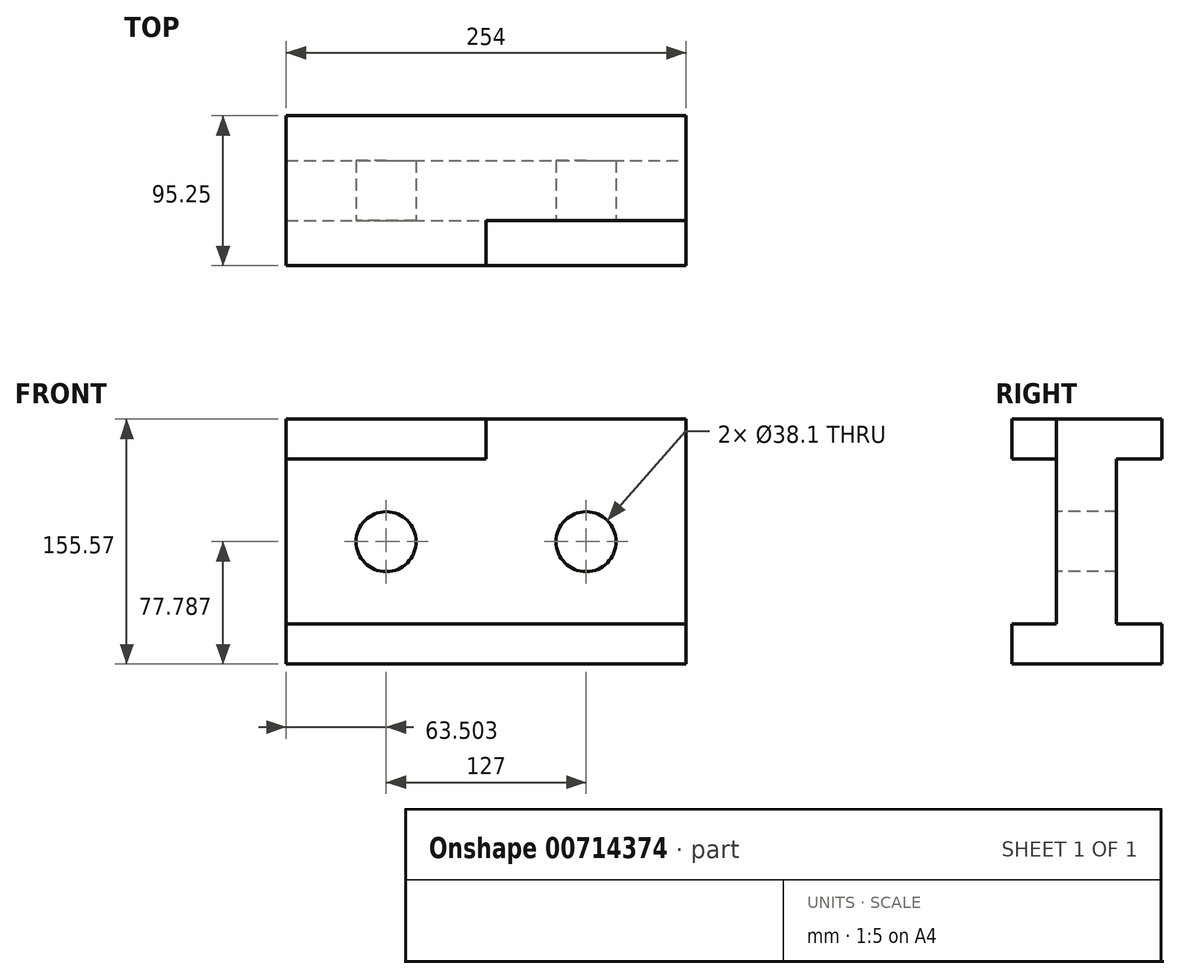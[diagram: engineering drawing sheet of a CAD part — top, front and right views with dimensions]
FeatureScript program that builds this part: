
annotation { "Feature Type Name" : "Feature", "Feature Type Description" : "" }
export const myFeature = defineFeature(function(context is Context, id is Id, definition is map)
    precondition{}
    {
        {
            var Q0;
            Q0=qCreatedBy(makeId("Front.planeOp"),FACE);
            var sketch = newSketch(context, id + "F0", { "sketchPlane" : qUnion([Q0])});
            skLineSegment(sketch, "E0.bottom", {"start": v(-135.4, 43.15) * mm, "end": v(118.6, 43.15) * mm});
            skLineSegment(sketch, "E0.top", {"start": v(-135.4, -112.42) * mm, "end": v(118.6, -112.42) * mm});
            skLineSegment(sketch, "E0.left", {"start": v(-135.4, 43.15) * mm, "end": v(-135.4, -112.42) * mm});
            skLineSegment(sketch, "E0.right", {"start": v(118.6, 43.15) * mm, "end": v(118.6, -112.42) * mm});
            skSolve(sketch);
        }
        {
            var Q0;
            Q0=qSketchRegion(id+"F0",true);
            extrude(context, id + "F1", {"entities" : qUnion([Q0]), "depth" : 95.25 * mm, "offsetDistance" : 25.4 * mm});
        }
        {
            var Q0;
            Q0=makeQuery(id+"F1.opExtrude","CAP_FACE",FACE,{"disambiguationData":[OSD([sQuery(id+"F0.wireOp",EDGE,"E0.bottom"),sQuery(id+"F0.wireOp",EDGE,"E0.top"),sQuery(id+"F0.wireOp",EDGE,"E0.left"),sQuery(id+"F0.wireOp",EDGE,"E0.right")])],"isStart":false});
            var sketch = newSketch(context, id + "F2", { "sketchPlane" : qUnion([Q0])});
            skLineSegment(sketch, "E1.bottom", {"start": v(-135.4, 17.75) * mm, "end": v(118.6, 17.75) * mm});
            skLineSegment(sketch, "E1.top", {"start": v(-135.4, -87.02) * mm, "end": v(118.6, -87.02) * mm});
            skLineSegment(sketch, "E1.left", {"start": v(-135.4, 17.75) * mm, "end": v(-135.4, -87.02) * mm});
            skLineSegment(sketch, "E1.right", {"start": v(118.6, 17.75) * mm, "end": v(118.6, -87.02) * mm});
            skSolve(sketch);
        }
        {
            var Q0;
            Q0=makeQuery(id+"F2.imprint","IMPRINT",FACE,{"disambiguationData":[TD([[makeQuery(id+"F2.imprint","IMPRINT",EDGE,{"derivedFrom":sQuery(id+"F2.wireOp",EDGE,"E1.bottom")}),-1.0]])]});
            extrude(context, id + "F3", {"entities" : qUnion([Q0]), "operationType" : NewBodyOperationType.REMOVE, "oppositeDirection" : true, "depth" : 28.57 * mm, "offsetDistance" : 25.4 * mm});
        }
        {
            var Q0;
            {var subQ0=sQuery(id+"F0.wireOp",EDGE,"E0.bottom");var subQ1=sQuery(id+"F0.wireOp",EDGE,"E0.right");var subQ2=sQuery(id+"F0.wireOp",EDGE,"E0.left");Q0=makeQuery(id+"F3.boolean.opBoolean","SPLIT",FACE,{"disambiguationData":[TD([makeQuery(id+"F1.opExtrude","SWEPT_FACE",FACE,{"disambiguationData":[OSD([subQ0])]})])],"derivedFrom":makeQuery(id+"F1.opExtrude","CAP_FACE",FACE,{"disambiguationData":[OSD([subQ0,sQuery(id+"F0.wireOp",EDGE,"E0.top"),subQ2,subQ1])],"isStart":false})});}
            var sketch = newSketch(context, id + "F4", { "sketchPlane" : qUnion([Q0])});
            skLineSegment(sketch, "E2.bottom", {"start": v(118.6, 17.75) * mm, "end": v(-8.4, 17.75) * mm});
            skLineSegment(sketch, "E2.top", {"start": v(118.6, 43.15) * mm, "end": v(-8.4, 43.15) * mm});
            skLineSegment(sketch, "E2.left", {"start": v(118.6, 17.75) * mm, "end": v(118.6, 43.15) * mm});
            skLineSegment(sketch, "E2.right", {"start": v(-8.4, 17.75) * mm, "end": v(-8.4, 43.15) * mm});
            skSolve(sketch);
        }
        {
            var Q0;
            Q0=qSketchRegion(id+"F4",true);
            extrude(context, id + "F5", {"entities" : qUnion([Q0]), "operationType" : NewBodyOperationType.REMOVE, "oppositeDirection" : true, "depth" : 28.57 * mm, "offsetDistance" : 25.4 * mm});
        }
        {
            var Q0;
            Q0=makeQuery(id+"F5.boolean.opBoolean","MERGE",FACE,{"derivedFrom":[makeQuery(id+"F3.boolean.opBoolean","COPY",FACE,{"derivedFrom":makeQuery(id+"F3.opExtrude","CAP_FACE",FACE,{"disambiguationData":[OSD([sQuery(id+"F2.wireOp",EDGE,"E1.bottom"),sQuery(id+"F2.wireOp",EDGE,"E1.top"),sQuery(id+"F2.wireOp",EDGE,"E1.left"),sQuery(id+"F2.wireOp",EDGE,"E1.right")])],"isStart":false})}),makeQuery(id+"F5.opExtrude","CAP_FACE",FACE,{"disambiguationData":[OSD([sQuery(id+"F4.wireOp",EDGE,"E2.bottom"),sQuery(id+"F4.wireOp",EDGE,"E2.top"),sQuery(id+"F4.wireOp",EDGE,"E2.left"),sQuery(id+"F4.wireOp",EDGE,"E2.right")])],"isStart":false})]});
            var sketch = newSketch(context, id + "F6", { "sketchPlane" : qUnion([Q0])});
            skCircle(sketch, "E3", {"center": v(-71.9, -34.63) * mm, "radius": 19.05 * mm});
            skCircle(sketch, "E4", {"center": v(55.1, -34.63) * mm, "radius": 19.05 * mm});
            skSolve(sketch);
        }
        {
            var Q0;
            Q0=makeQuery(id+"F6.imprint","IMPRINT",FACE,{"disambiguationData":[TD([[makeQuery(id+"F6.imprint","IMPRINT",EDGE,{"derivedFrom":sQuery(id+"F6.wireOp",EDGE,"E4")}),1.0]])]});
            var Q1;
            Q1=makeQuery(id+"F6.imprint","IMPRINT",FACE,{"disambiguationData":[TD([[makeQuery(id+"F6.imprint","IMPRINT",EDGE,{"derivedFrom":sQuery(id+"F6.wireOp",EDGE,"E3")}),1.0]])]});
            extrude(context, id + "F7", {"entities" : qUnion([Q0, Q1]), "operationType" : NewBodyOperationType.REMOVE, "endBound" : BoundingType.THROUGH_ALL, "oppositeDirection" : true, "depth" : 25.4 * mm, "offsetDistance" : 25.4 * mm});
        }
        {
            var Q0;
            Q0=makeQuery(id+"F1.opExtrude","SWEPT_FACE",FACE,{"disambiguationData":[OSD([sQuery(id+"F0.wireOp",EDGE,"E0.right")])]});
            var sketch = newSketch(context, id + "F8", { "sketchPlane" : qUnion([Q0])});
            skLineSegment(sketch, "E5.bottom", {"start": v(0, -87.02) * mm, "end": v(-28.57, -87.02) * mm});
            skLineSegment(sketch, "E5.top", {"start": v(0, 17.75) * mm, "end": v(-28.58, 17.75) * mm});
            skLineSegment(sketch, "E5.left", {"start": v(0, -87.02) * mm, "end": v(0, 17.75) * mm});
            skLineSegment(sketch, "E5.right", {"start": v(-28.57, -87.02) * mm, "end": v(-28.58, 17.75) * mm});
            skSolve(sketch);
        }
        {
            var Q0;
            Q0=makeQuery(id+"F8.imprint","IMPRINT",FACE,{"disambiguationData":[TD([[makeQuery(id+"F8.imprint","IMPRINT",EDGE,{"derivedFrom":sQuery(id+"F8.wireOp",EDGE,"E5.bottom")}),-1.0]])]});
            extrude(context, id + "F9", {"entities" : qUnion([Q0]), "operationType" : NewBodyOperationType.REMOVE, "endBound" : BoundingType.THROUGH_ALL, "oppositeDirection" : true, "depth" : 25.4 * mm, "offsetDistance" : 25.4 * mm});
        }
    });
